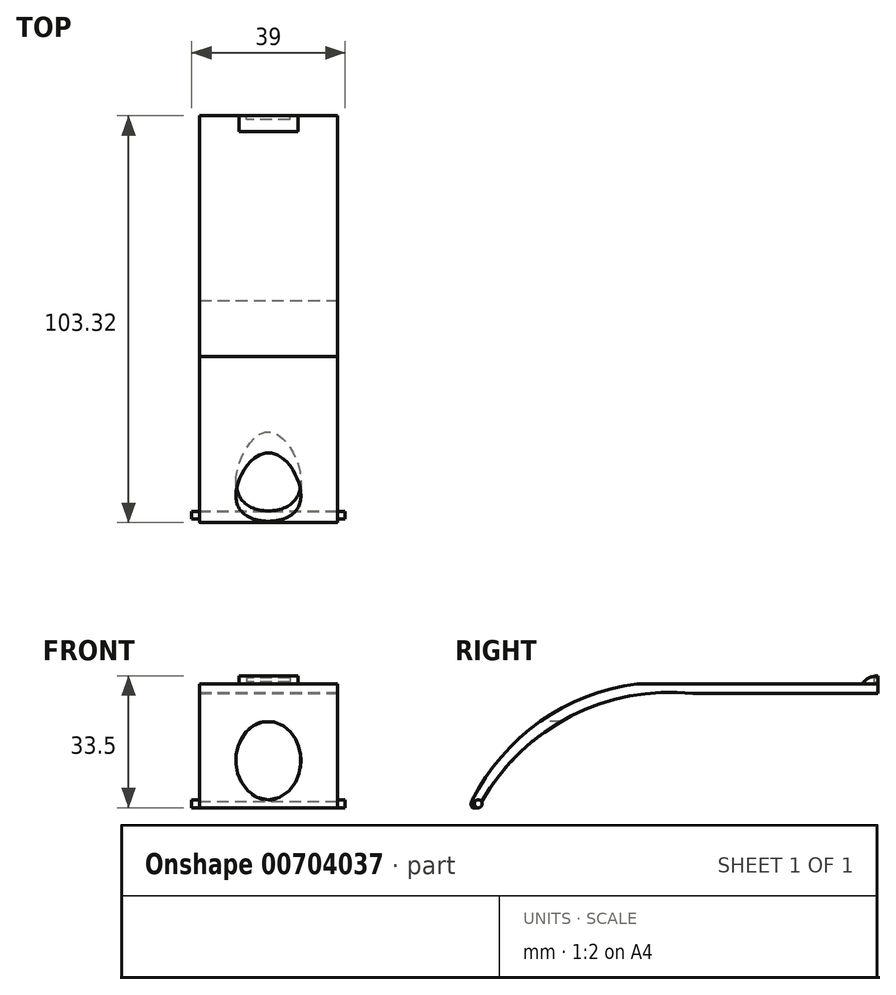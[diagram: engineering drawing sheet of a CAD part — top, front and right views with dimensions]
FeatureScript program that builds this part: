
annotation { "Feature Type Name" : "Feature", "Feature Type Description" : "" }
export const myFeature = defineFeature(function(context is Context, id is Id, definition is map)
    precondition{}
    {
        {
            var Q0;
            Q0=qCreatedBy(makeId("Top.planeOp"),FACE);
            var sketch = newSketch(context, id + "F0", { "sketchPlane" : qUnion([Q0])});
            skLineSegment(sketch, "E0.bottom", {"start": v(-17.4, 3.7) * mm, "end": v(17.6, 3.7) * mm});
            skLineSegment(sketch, "E0.top", {"start": v(-17.4, -53.3) * mm, "end": v(17.6, -53.3) * mm});
            skLineSegment(sketch, "E0.left", {"start": v(-17.4, 3.7) * mm, "end": v(-17.4, -53.3) * mm});
            skLineSegment(sketch, "E0.right", {"start": v(17.6, 3.7) * mm, "end": v(17.6, -53.3) * mm});
            skSolve(sketch);
        }
        {
            var Q0;
            Q0=makeQuery(id+"F0.imprint","IMPRINT",FACE,{"disambiguationData":[TD([[makeQuery(id+"F0.imprint","IMPRINT",EDGE,{"derivedFrom":sQuery(id+"F0.wireOp",EDGE,"E0.bottom")}),-1.0]])]});
            extrude(context, id + "F1", {"entities" : qUnion([Q0]), "depth" : 31.5 * mm, "offsetDistance" : 25 * mm});
        }
        {
            var Q0;
            Q0=makeQuery(id+"F1.opExtrude","SWEPT_FACE",FACE,{"disambiguationData":[OSD([sQuery(id+"F0.wireOp",EDGE,"E0.right")])]});
            var sketch = newSketch(context, id + "F2", { "sketchPlane" : qUnion([Q0])});
            skArc(sketch, "E1", {"start": v(3.7, 31.5) * mm, "mid": v(-29.97, 25.1) * mm, "end": v(-53.3, 0) * mm});
            skSolve(sketch);
        }
        {
            var Q0;
            Q0=makeQuery(id+"F1.opExtrude","SWEPT_FACE",FACE,{"disambiguationData":[OSD([sQuery(id+"F0.wireOp",EDGE,"E0.top")])]});
            var sketch = newSketch(context, id + "F3", { "sketchPlane" : qUnion([Q0])});
            skEllipse(sketch, "E2", {"center": v(0.1, 12) * mm, "majorRadius": 10 * mm, "minorRadius": 8.25 * mm, "majorAxis": v(0, -1)});
            skSolve(sketch);
        }
        {
            var Q0;
            Q0=makeQuery(id+"F3.imprint","IMPRINT",FACE,{"disambiguationData":[TD([[makeQuery(id+"F3.imprint","IMPRINT",EDGE,{"derivedFrom":sQuery(id+"F3.wireOp",EDGE,"E2")}),1.0]])]});
            extrude(context, id + "F4", {"entities" : qUnion([Q0]), "operationType" : NewBodyOperationType.REMOVE, "endBound" : BoundingType.THROUGH_ALL, "oppositeDirection" : true, "depth" : 25 * mm, "offsetDistance" : 25 * mm});
        }
        {
            var Q0;
            Q0=makeQuery(id+"F2.imprint","IMPRINT",FACE,{"disambiguationData":[TD([[makeQuery(id+"F2.imprint","IMPRINT",EDGE,{"derivedFrom":sQuery(id+"F2.wireOp",EDGE,"E1")}),-1.0]])]});
            extrude(context, id + "F5", {"entities" : qUnion([Q0]), "operationType" : NewBodyOperationType.REMOVE, "endBound" : BoundingType.THROUGH_ALL, "oppositeDirection" : true, "depth" : 25 * mm, "offsetDistance" : 25 * mm});
        }
        {
            var Q0;
            Q0=makeQuery(id+"F1.opExtrude","SWEPT_FACE",FACE,{"disambiguationData":[OSD([sQuery(id+"F0.wireOp",EDGE,"E0.right")])]});
            var sketch = newSketch(context, id + "F6", { "sketchPlane" : qUnion([Q0])});
            skArc(sketch, "E3", {"start": v(3.7, 29) * mm, "mid": v(-28, 22.87) * mm, "end": v(-50.8, 0) * mm});
            skSolve(sketch);
        }
        {
            var Q0;
            {var subQ0=sQuery(id+"F6.wireOp",EDGE,"E3");Q0=makeQuery(id+"F6.imprint","IMPRINT",FACE,{"disambiguationData":[TD([[makeQuery(id+"F6.imprint","IMPRINT",EDGE,{"derivedFrom":subQ0}),1.0]])]});}
            extrude(context, id + "F7", {"entities" : qUnion([Q0]), "operationType" : NewBodyOperationType.REMOVE, "endBound" : BoundingType.THROUGH_ALL, "oppositeDirection" : true, "depth" : 25 * mm, "offsetDistance" : 25 * mm});
        }
        {
            var Q0;
            Q0=makeQuery(id+"F1.opExtrude","SWEPT_FACE",FACE,{"disambiguationData":[OSD([sQuery(id+"F0.wireOp",EDGE,"E0.right")])]});
            var sketch = newSketch(context, id + "F8", { "sketchPlane" : qUnion([Q0])});
            skCircle(sketch, "E4", {"center": v(-50.8, 1) * mm, "radius": 1 * mm});
            skSolve(sketch);
        }
        {
            var Q0;
            {var subQ0=sQuery(id+"F8.wireOp",EDGE,"E4");var subQ1=makeQuery(id+"F7.boolean.opBoolean","COPY",EDGE,{"derivedFrom":makeQuery(id+"F7.opExtrude","CAP_EDGE",EDGE,{"disambiguationData":[OSD([sQuery(id+"F6.wireOp",EDGE,"E3")])],"isStart":true})});var subQ3=makeQuery(id+"F8.imprint","INTERSECT",VERTEX,{"derivedFrom":[subQ1,subQ0]});Q0=makeQuery(id+"F8.imprint","IMPRINT",FACE,{"disambiguationData":[TD([[makeQuery(id+"F8.imprint","IMPRINT",EDGE,{"disambiguationData":[TD([[subQ3,-1.0]])],"derivedFrom":subQ0}),1.0]])]});}
            var Q1;
            {var subQ0=sQuery(id+"F8.wireOp",EDGE,"E4");var subQ1=makeQuery(id+"F7.boolean.opBoolean","COPY",EDGE,{"derivedFrom":makeQuery(id+"F7.opExtrude","CAP_EDGE",EDGE,{"disambiguationData":[OSD([sQuery(id+"F6.wireOp",EDGE,"E3")])],"isStart":true})});var subQ3=makeQuery(id+"F8.imprint","INTERSECT",VERTEX,{"derivedFrom":[subQ1,subQ0]});Q1=makeQuery(id+"F8.imprint","IMPRINT",FACE,{"disambiguationData":[TD([[makeQuery(id+"F8.imprint","IMPRINT",EDGE,{"disambiguationData":[TD([[subQ3,1.0]])],"derivedFrom":subQ0}),1.0]])]});}
            extrude(context, id + "F9", {"entities" : qUnion([Q0, Q1]), "operationType" : NewBodyOperationType.ADD, "depth" : 2 * mm, "offsetDistance" : 25 * mm, "hasSecondDirection" : true, "secondDirectionOppositeDirection" : true, "secondDirectionDepth" : 37 * mm});
        }
        {
            var Q0;
            Q0=makeQuery(id+"F1.opExtrude","SWEPT_FACE",FACE,{"disambiguationData":[OSD([sQuery(id+"F0.wireOp",EDGE,"E0.right")])]});
            var sketch = newSketch(context, id + "F10", { "sketchPlane" : qUnion([Q0])});
            skCircle(sketch, "E5", {"center": v(-50.8, 1) * mm, "radius": 1.82 * mm});
            skSolve(sketch);
        }
        {
            var Q0;
            {var subQ0=sQuery(id+"F10.wireOp",EDGE,"E5");var subQ1=makeQuery(id+"F5.boolean.opBoolean","COPY",EDGE,{"derivedFrom":makeQuery(id+"F5.opExtrude","CAP_EDGE",EDGE,{"disambiguationData":[OSD([sQuery(id+"F2.wireOp",EDGE,"E1")])],"isStart":true})});var subQ2=makeQuery(id+"F10.imprint","INTERSECT",VERTEX,{"derivedFrom":[subQ1,subQ0]});Q0=makeQuery(id+"F10.imprint","IMPRINT",FACE,{"disambiguationData":[TD([[makeQuery(id+"F10.imprint","IMPRINT",EDGE,{"disambiguationData":[TD([[subQ2,-1.0]])],"derivedFrom":subQ0}),-1.0]])]});}
            extrude(context, id + "F11", {"entities" : qUnion([Q0]), "operationType" : NewBodyOperationType.REMOVE, "endBound" : BoundingType.THROUGH_ALL, "oppositeDirection" : true, "depth" : 25 * mm, "offsetDistance" : 25 * mm});
        }
        {
            var Q0;
            Q0=makeQuery(id+"F1.opExtrude","SWEPT_FACE",FACE,{"disambiguationData":[OSD([sQuery(id+"F0.wireOp",EDGE,"E0.bottom")])]});
            extrude(context, id + "F12", {"entities" : qUnion([Q0]), "operationType" : NewBodyOperationType.ADD, "depth" : 47 * mm, "offsetDistance" : 25 * mm});
        }
        {
            var Q0;
            {var subQ0=sQuery(id+"F0.wireOp",EDGE,"E0.bottom");Q0=makeQuery(id+"F12.boolean.opBoolean","MERGE",FACE,{"derivedFrom":[makeQuery(id+"F1.opExtrude","CAP_FACE",FACE,{"disambiguationData":[OSD([subQ0,sQuery(id+"F0.wireOp",EDGE,"E0.top"),sQuery(id+"F0.wireOp",EDGE,"E0.left"),sQuery(id+"F0.wireOp",EDGE,"E0.right")])],"isStart":false}),makeQuery(id+"F12.opExtrude","SWEPT_FACE",FACE,{"disambiguationData":[OSD([subQ0])]})]});}
            var sketch = newSketch(context, id + "F13", { "sketchPlane" : qUnion([Q0])});
            skLineSegment(sketch, "E6.bottom", {"start": v(-7.4, 50.7) * mm, "end": v(7.6, 50.7) * mm});
            skLineSegment(sketch, "E6.top", {"start": v(-7.4, 46.7) * mm, "end": v(7.6, 46.7) * mm});
            skLineSegment(sketch, "E6.left", {"start": v(-7.4, 50.7) * mm, "end": v(-7.4, 46.7) * mm});
            skLineSegment(sketch, "E6.right", {"start": v(7.6, 50.7) * mm, "end": v(7.6, 46.7) * mm});
            skSolve(sketch);
        }
        {
            var Q0;
            Q0=makeQuery(id+"F13.imprint","IMPRINT",FACE,{"disambiguationData":[TD([[makeQuery(id+"F13.imprint","IMPRINT",EDGE,{"derivedFrom":sQuery(id+"F13.wireOp",EDGE,"E6.bottom")}),-1.0]])]});
            extrude(context, id + "F14", {"entities" : qUnion([Q0]), "operationType" : NewBodyOperationType.ADD, "depth" : 2 * mm, "offsetDistance" : 25 * mm});
        }
        {
            var Q0;
            Q0=makeQuery(id+"F14.opExtrude","CAP_EDGE",EDGE,{"disambiguationData":[OSD([sQuery(id+"F13.wireOp",EDGE,"E6.top")])],"isStart":false});
            fillet(context, id + "F15", {"entities" : qUnion([Q0]), "radius" : 5 * mm, "tangentPropagation" : true, "allowEdgeOverflow" : false});
        }
        {
            var Q0;
            Q0=makeQuery(id+"F14.boolean.opBoolean","MERGE",FACE,{"derivedFrom":[makeQuery(id+"F12.opExtrude","CAP_FACE",FACE,{"disambiguationData":[OSD([sQuery(id+"F0.wireOp",EDGE,"E0.bottom")])],"isStart":false}),makeQuery(id+"F14.opExtrude","SWEPT_FACE",FACE,{"disambiguationData":[OSD([sQuery(id+"F13.wireOp",EDGE,"E6.bottom")])]})]});
            var sketch = newSketch(context, id + "F16", { "sketchPlane" : qUnion([Q0])});
            skLineSegment(sketch, "E7.bottom", {"start": v(-5.6, 33) * mm, "end": v(5.4, 33) * mm});
            skLineSegment(sketch, "E7.top", {"start": v(-5.6, 32) * mm, "end": v(5.4, 32) * mm});
            skLineSegment(sketch, "E7.left", {"start": v(-5.6, 33) * mm, "end": v(-5.6, 32) * mm});
            skLineSegment(sketch, "E7.right", {"start": v(5.4, 33) * mm, "end": v(5.4, 32) * mm});
            skSolve(sketch);
        }
        {
            var Q0;
            Q0=makeQuery(id+"F16.imprint","IMPRINT",FACE,{"disambiguationData":[TD([[makeQuery(id+"F16.imprint","IMPRINT",EDGE,{"derivedFrom":sQuery(id+"F16.wireOp",EDGE,"E7.bottom")}),-1.0]])]});
            extrude(context, id + "F17", {"entities" : qUnion([Q0]), "operationType" : NewBodyOperationType.REMOVE, "oppositeDirection" : true, "depth" : 1 * mm, "offsetDistance" : 25 * mm});
        }
    });
